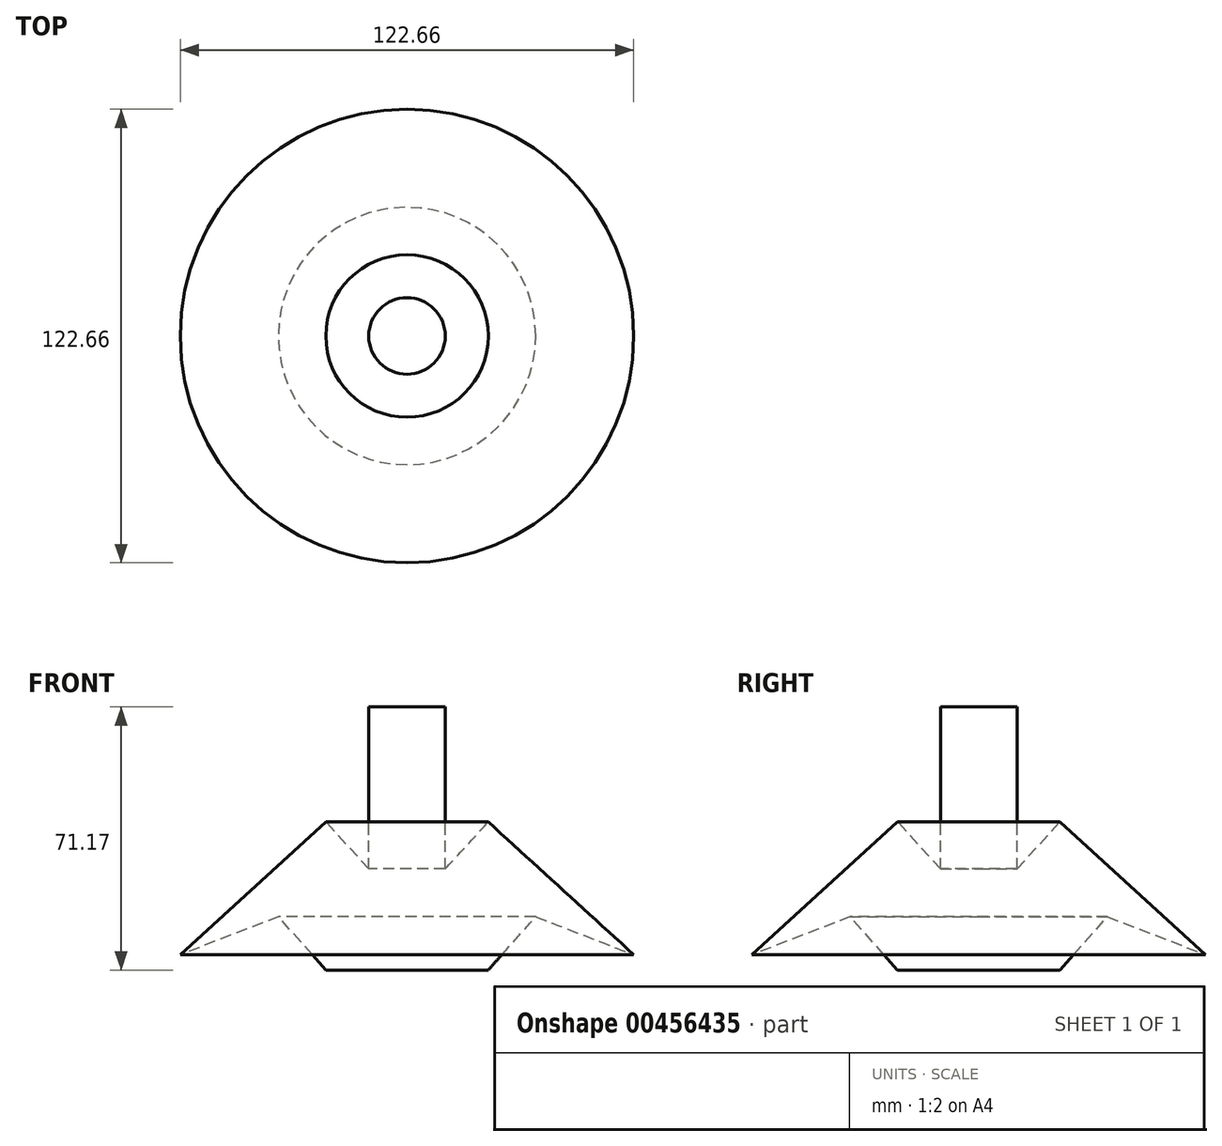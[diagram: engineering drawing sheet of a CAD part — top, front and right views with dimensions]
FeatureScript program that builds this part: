
annotation { "Feature Type Name" : "Feature", "Feature Type Description" : "" }
export const myFeature = defineFeature(function(context is Context, id is Id, definition is map)
    precondition{}
    {
        {
            var Q0;
            Q0=qCreatedBy(makeId("Front.planeOp"),FACE);
            var sketch = newSketch(context, id + "F0", { "sketchPlane" : qUnion([Q0])});
            skLineSegment(sketch, "E0", {"start": v(0, 0) * mm, "end": v(21.96, 0) * mm});
            skLineSegment(sketch, "E1", {"start": v(21.96, 0) * mm, "end": v(34.8, 14.4) * mm});
            skLineSegment(sketch, "E2", {"start": v(34.8, 14.4) * mm, "end": v(61.33, 4.14) * mm});
            skLineSegment(sketch, "E3", {"start": v(61.33, 4.14) * mm, "end": v(21.96, 40.08) * mm});
            skLineSegment(sketch, "E4", {"start": v(21.96, 40.08) * mm, "end": v(10.36, 27.37) * mm});
            skLineSegment(sketch, "E5", {"start": v(10.36, 27.37) * mm, "end": v(10.36, 71.17) * mm});
            skLineSegment(sketch, "E6", {"start": v(10.36, 71.17) * mm, "end": v(0, 71.17) * mm});
            skLineSegment(sketch, "E7", {"start": v(0, 71.17) * mm, "end": v(0, 0) * mm});
            skSolve(sketch);
        }
        {
            var Q0;
            Q0=makeQuery(id+"F0.imprint","IMPRINT",FACE,{"disambiguationData":[TD([[makeQuery(id+"F0.imprint","IMPRINT",EDGE,{"derivedFrom":sQuery(id+"F0.wireOp",EDGE,"E0")}),1.0]])]});
            var Q1;
            Q1=sQuery(id+"F0.wireOp",EDGE,"E7");
            revolve(context, id + "F1", {"entities" : qUnion([Q0]), "axis" : qUnion([Q1]), "revolveType" : RevolveType.FULL});
        }
    });
